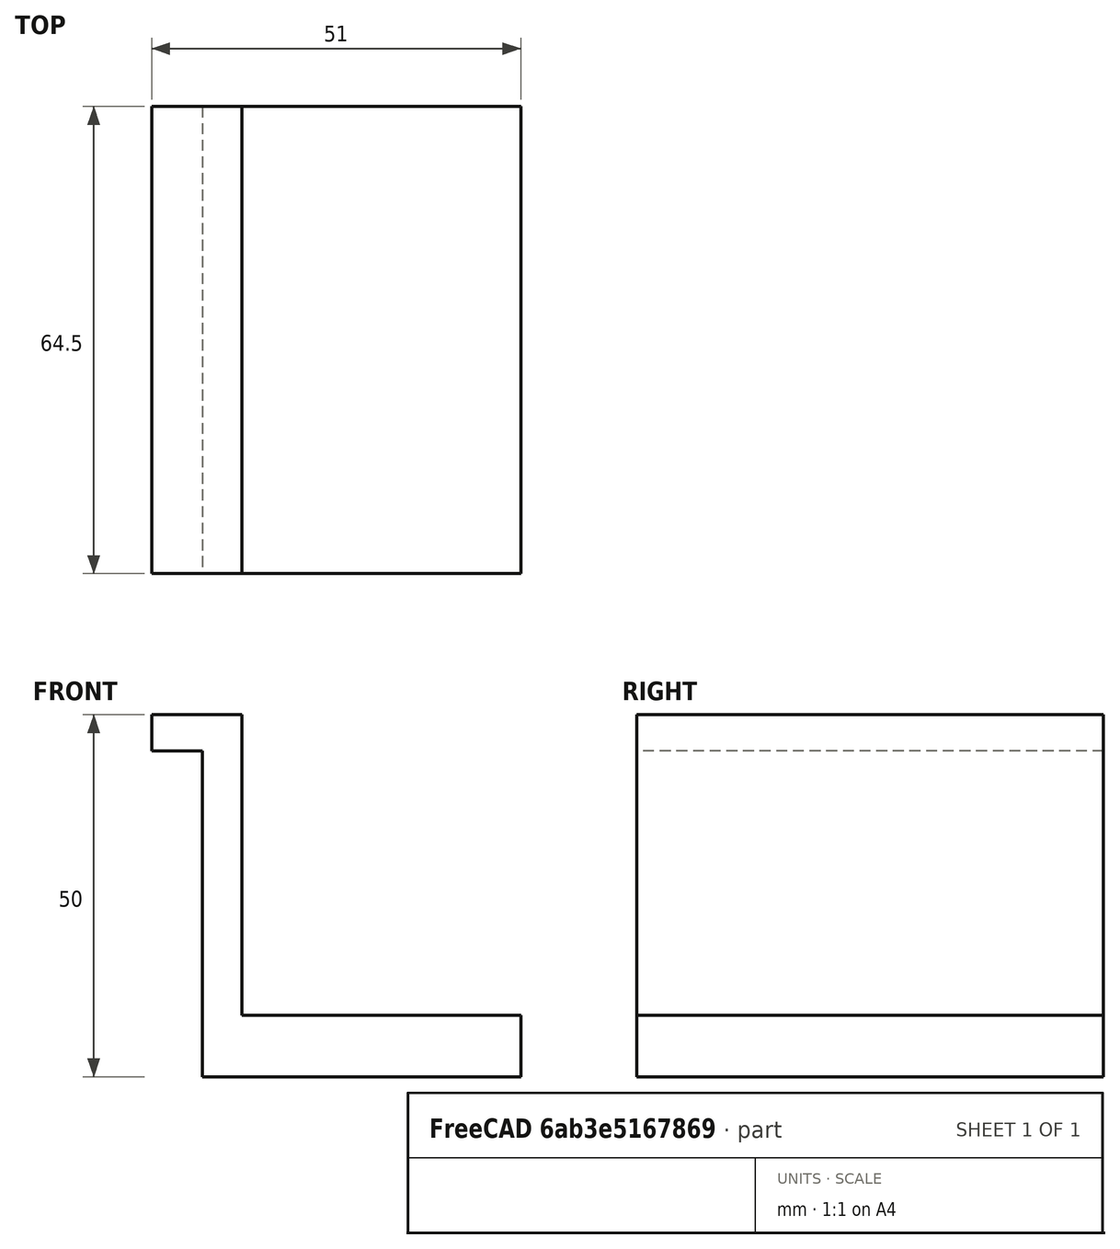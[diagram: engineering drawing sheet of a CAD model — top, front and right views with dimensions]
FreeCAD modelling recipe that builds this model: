
FCSTD DOCUMENT  (FreeCAD 0.21R33771 (Git))
Label: wellhofer-frame
License: All rights reserved
LicenseURL: https://en.wikipedia.org/wiki/All_rights_reserved
objects: Sketcher::SketchObject×1, PartDesign::Pad×1, PartDesign::Body×1
note: 4 computed .brp shape members not serialized (recipe doc carries the construction recipe); baked Part::Feature solids carry a one-line shape summary decoded from their .brp

FEATURE [Sketcher::SketchObject] Sketch
  FullyConstrained = true
  MapMode = 5
  Placement = pos=(0,0,0) rot=(1,0,0;1.5708rad)
  Support = -> [XZ_Plane]
  sketch-geometry (8):
    g0: LineSegment StartX=0.0458536 StartY=-0.00625433 StartZ=0 EndX=0.0458536 EndY=44.9937 EndZ=0
    g1: LineSegment StartX=-6.95415 StartY=44.9937 StartZ=0 EndX=0.0458536 EndY=44.9937 EndZ=0
    g2: LineSegment StartX=-6.95415 StartY=44.9937 StartZ=0 EndX=-6.95415 EndY=49.9937 EndZ=0
    g3: LineSegment StartX=5.54585 StartY=49.9937 StartZ=0 EndX=5.54585 EndY=8.49375 EndZ=0
    g4: LineSegment StartX=5.54585 StartY=8.49375 StartZ=0 EndX=44.0459 EndY=8.49375 EndZ=0
    g5: LineSegment StartX=44.0459 StartY=8.49375 StartZ=0 EndX=44.0459 EndY=-0.00625433 EndZ=0
    g6: LineSegment StartX=44.0459 StartY=-0.00625433 StartZ=0 EndX=0.0458536 EndY=-0.00625433 EndZ=0
    g7: LineSegment StartX=-6.95415 StartY=49.9937 StartZ=0 EndX=5.54585 EndY=49.9937 EndZ=0
  constraints (23):
    c: Coincident(g1,g0)
    c: Horizontal(g1)
    c: Coincident(g2,g1)
    c: Vertical(g2)
    c: Coincident(g4,g3)
    c: Horizontal(g4)
    c: Coincident(g5,g4)
    c: Vertical(g5)
    c: Coincident(g6,g5)
    c: Coincident(g6,g0)
    c: Horizontal(g6)
    c: Vertical(g0)
    c: Vertical(g3)
    c: Coincident(g7,g2)
    c: Coincident(g7,g3)
    c: Horizontal(g7)
    c: DistanceX(g7,g7) = 12.5
    c: DistanceX(g1,g1) = 7
    c: DistanceX(g4,g4) = 38.5
    c: DistanceY(g0,g0) = 45
    c: DistanceY(g5,g5) = 8.5
    c: DistanceY(g2,g2) = 5
    c: Block(g0)
FEATURE [PartDesign::Pad] Pad
  Direction = (0,-1,-2e-16)
  Length = 64.5
  Length2 = 10
  Placement = pos=(0,0,0) rot=(1,0,0;1.5708rad)
  Profile = -> Sketch
  ReferenceAxis = -> Sketch [N_Axis]
  Type = 0
FEATURE [PartDesign::Body] Body  label="part-frame-right"
  Group = -> [Sketch,Pad]
  Origin = -> Origin
  Tip = -> Pad
